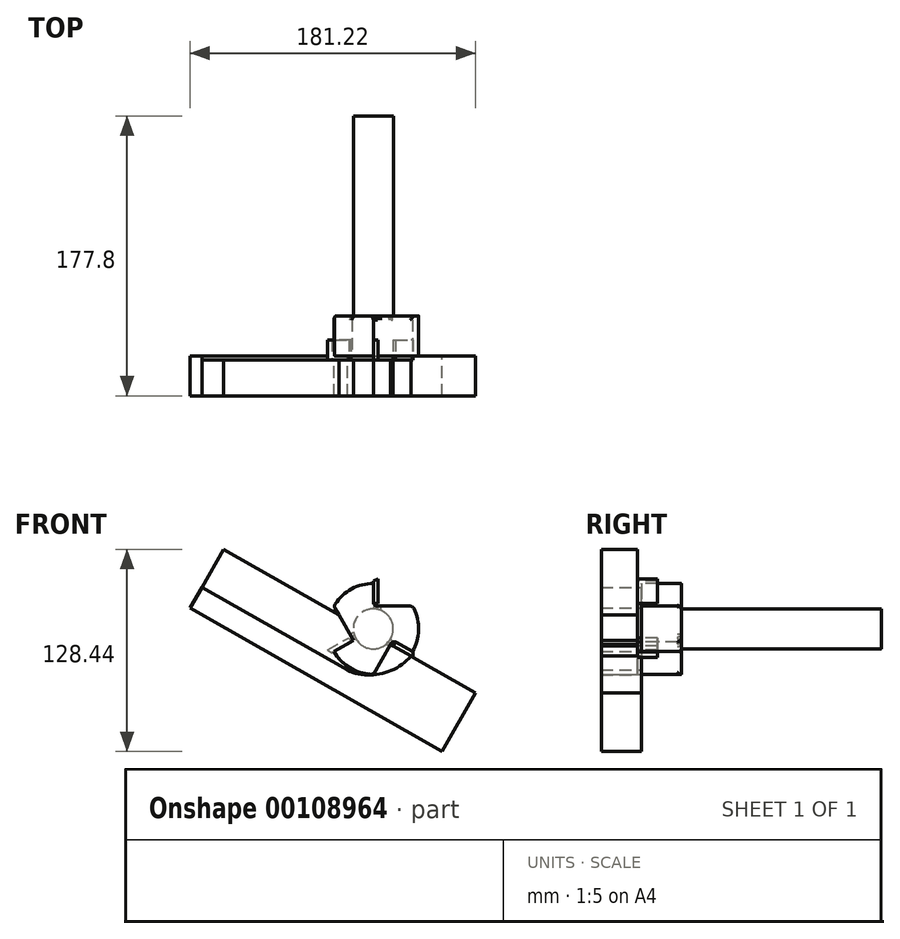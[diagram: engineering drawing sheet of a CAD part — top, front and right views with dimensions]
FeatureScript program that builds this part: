
annotation { "Feature Type Name" : "Feature", "Feature Type Description" : "" }
export const myFeature = defineFeature(function(context is Context, id is Id, definition is map)
    precondition{}
    {
        {
            var Q0;
            Q0=qCreatedBy(makeId("Front.planeOp"),FACE);
            var sketch = newSketch(context, id + "F0", { "sketchPlane" : qUnion([Q0])});
            skArc(sketch, "E0", {"start": v(-24.99, -14.43) * mm, "mid": v(-14.43, -24.99) * mm, "end": v(0, -28.85) * mm});
            skLineSegment(sketch, "E1", {"start": v(0, 14.43) * mm, "end": v(0, 28.85) * mm});
            skLineSegment(sketch, "E2", {"start": v(12.5, -7.21) * mm, "end": v(24.99, -14.43) * mm});
            skLineSegment(sketch, "E3", {"start": v(-12.5, -7.21) * mm, "end": v(-24.99, -14.43) * mm});
            skLineSegment(sketch, "E4", {"start": v(12.5, -7.21) * mm, "end": v(0, -28.85) * mm});
            skLineSegment(sketch, "E5", {"start": v(-12.5, -7.21) * mm, "end": v(-24.99, 14.43) * mm});
            skLineSegment(sketch, "E6", {"start": v(0, 14.43) * mm, "end": v(24.99, 14.43) * mm});
            skArc(sketch, "E7.trimOffspring", {"start": v(24.99, -14.43) * mm, "mid": v(28.85, 0) * mm, "end": v(24.99, 14.43) * mm});
            skArc(sketch, "E8.trimOffspring", {"start": v(0, 28.85) * mm, "mid": v(-14.43, 24.99) * mm, "end": v(-24.99, 14.43) * mm});
            skLineSegment(sketch, "E9", {"start": v(-24.99, -14.43) * mm, "end": v(-26.29, -15.16) * mm});
            skLineSegment(sketch, "E10", {"start": v(-29.06, -13.3) * mm, "end": v(-15.52, -5.64) * mm});
            skLineSegment(sketch, "E11", {"start": v(-15.52, -5.64) * mm, "end": v(-14.1, -8.14) * mm});
            skLineSegment(sketch, "E12", {"start": v(0, 28.85) * mm, "end": v(0, 30.35) * mm});
            skLineSegment(sketch, "E13", {"start": v(3, 31.84) * mm, "end": v(3, 16.29) * mm});
            skLineSegment(sketch, "E14", {"start": v(3, 16.29) * mm, "end": v(0, 16.29) * mm});
            skLineSegment(sketch, "E15", {"start": v(24.99, -14.43) * mm, "end": v(25.36, -14.63) * mm});
            skLineSegment(sketch, "E16", {"start": v(25.18, -17.97) * mm, "end": v(12.56, -10.9) * mm});
            skLineSegment(sketch, "E17", {"start": v(12.56, -10.9) * mm, "end": v(14.1, -8.14) * mm});
            skLineSegment(sketch, "E18", {"start": v(-29.06, -13.3) * mm, "end": v(-26.29, -15.16) * mm});
            skLineSegment(sketch, "E19", {"start": v(25.18, -17.97) * mm, "end": v(25.36, -14.63) * mm});
            skLineSegment(sketch, "E20", {"start": v(3, 31.84) * mm, "end": v(0, 30.35) * mm});
            skLineSegment(sketch, "E21", {"start": v(25.18, -17.97) * mm, "end": v(64.89, -40.59) * mm});
            skLineSegment(sketch, "E22", {"start": v(-16.45, -26.15) * mm, "end": v(-108.78, 26.45) * mm});
            skEllipticalArc(sketch, "E23.trimOffspring", {});
            skLineSegment(sketch, "E24", {"start": v(-108.78, 26.45) * mm, "end": v(-116.33, 13.2) * mm});
            skLineSegment(sketch, "E25", {"start": v(-116.33, 13.2) * mm, "end": v(43.62, -77.92) * mm});
            skLineSegment(sketch, "E26", {"start": v(43.62, -77.92) * mm, "end": v(64.89, -40.59) * mm});
            skLineSegment(sketch, "E27", {"start": v(-108.78, 26.45) * mm, "end": v(-95.06, 50.52) * mm});
            skLineSegment(sketch, "E28", {"start": v(-95.06, 50.52) * mm, "end": v(23.9, -17.25) * mm});
            const initialGuessF0  = {"E23.trimOffspring": [0, 0, -0.9093747763503883, -0.41597778322607715, 0.03196105381302888, 0.028787567373013776, 0.6291453285315938, 2.04370583019782]};
            skSetInitialGuess(sketch, initialGuessF0);
            skSolve(sketch);
        }
        {
            var Q0;
            {var subQ0=sQuery(id+"F0.wireOp",EDGE,"E4");var subQ1=sQuery(id+"F0.wireOp",EDGE,"E0");var subQ2=makeQuery(id+"F0.imprint","INTERSECT",VERTEX,{"derivedFrom":[subQ1,subQ0]});Q0=makeQuery(id+"F0.imprint","IMPRINT",FACE,{"disambiguationData":[TD([[makeQuery(id+"F0.imprint","IMPRINT",EDGE,{"disambiguationData":[TD([[subQ2,1.0]])],"derivedFrom":subQ1}),1.0]])]});}
            var Q1;
            {var subQ11=sQuery(id+"F0.wireOp",EDGE,"E5");Q1=makeQuery(id+"F0.imprint","IMPRINT",FACE,{"disambiguationData":[TD([[makeQuery(id+"F0.imprint","IMPRINT",EDGE,{"derivedFrom":subQ11}),-1.0]])]});}
            var Q2;
            {var subQ0=sQuery(id+"F0.wireOp",EDGE,"E0");var subQ1=sQuery(id+"F0.wireOp",EDGE,"E4");var subQ2=makeQuery(id+"F0.imprint","INTERSECT",VERTEX,{"derivedFrom":[subQ1,subQ0]});Q2=makeQuery(id+"F0.imprint","IMPRINT",FACE,{"disambiguationData":[TD([[makeQuery(id+"F0.imprint","IMPRINT",EDGE,{"disambiguationData":[TD([[subQ2,1.0]])],"derivedFrom":subQ1}),-1.0]])]});}
            var Q3;
            {var subQ3=sQuery(id+"F0.wireOp",EDGE,"E6");Q3=makeQuery(id+"F0.imprint","IMPRINT",FACE,{"disambiguationData":[TD([[makeQuery(id+"F0.imprint","IMPRINT",EDGE,{"derivedFrom":subQ3}),-1.0]])]});}
            extrude(context, id + "F1", {"entities" : qUnion([Q0, Q1, Q2, Q3]), "oppositeDirection" : true, "depth" : 25.4 * mm});
        }
        {
            var Q0;
            {var subQ1=sQuery(id+"F0.wireOp",EDGE,"E15");Q0=makeQuery(id+"F0.imprint","IMPRINT",FACE,{"disambiguationData":[TD([[makeQuery(id+"F0.imprint","IMPRINT",EDGE,{"derivedFrom":subQ1}),-1.0]])]});}
            var Q1;
            {var subQ1=sQuery(id+"F0.wireOp",EDGE,"E12");Q1=makeQuery(id+"F0.imprint","IMPRINT",FACE,{"disambiguationData":[TD([[makeQuery(id+"F0.imprint","IMPRINT",EDGE,{"derivedFrom":subQ1}),-1.0]])]});}
            var Q2;
            {var subQ1=sQuery(id+"F0.wireOp",EDGE,"E9");Q2=makeQuery(id+"F0.imprint","IMPRINT",FACE,{"disambiguationData":[TD([[makeQuery(id+"F0.imprint","IMPRINT",EDGE,{"derivedFrom":subQ1}),-1.0]])]});}
            extrude(context, id + "F2", {"entities" : qUnion([Q0, Q1, Q2]), "oppositeDirection" : true, "depth" : 10.16 * mm, "hasSecondDirection" : true, "secondDirectionOppositeDirection" : false, "secondDirectionDepth" : 2.54 * mm});
        }
        {
            var Q0;
            Q0=makeQuery(id+"F1.opExtrude","CAP_FACE",FACE,{"disambiguationData":[OSD([sQuery(id+"F0.wireOp",EDGE,"E1"),sQuery(id+"F0.wireOp",EDGE,"E2"),sQuery(id+"F0.wireOp",EDGE,"E3"),sQuery(id+"F0.wireOp",EDGE,"E4"),sQuery(id+"F0.wireOp",EDGE,"E5"),sQuery(id+"F0.wireOp",EDGE,"E6"),sQuery(id+"F0.wireOp",EDGE,"E7.trimOffspring"),sQuery(id+"F0.wireOp",EDGE,"E0"),sQuery(id+"F0.wireOp",EDGE,"E8.trimOffspring")])],"isStart":false});
            var sketch = newSketch(context, id + "F3", { "sketchPlane" : qUnion([Q0])});
            skCircle(sketch, "E29", {"center": v(0, 0) * mm, "radius": 12.7 * mm});
            skSolve(sketch);
        }
        {
            var Q0;
            Q0 = qSketchRegion(id + "F3", true);
            var Q1;
            Q1=makeQuery(id+"F3.imprint","IMPRINT",FACE,{"disambiguationData":[TD([[makeQuery(id+"F3.imprint","IMPRINT",EDGE,{"derivedFrom":sQuery(id+"F3.wireOp",EDGE,"E29")}),1.0]])]});
            extrude(context, id + "F4", {"entities" : qUnion([Q0, Q1]), "operationType" : NewBodyOperationType.ADD, "depth" : 127 * mm});
        }
        {
            var Q0;
            Q0=makeQuery(id+"F1.opExtrude","CAP_EDGE",EDGE,{"disambiguationData":[OSD([sQuery(id+"F0.wireOp",EDGE,"E8.trimOffspring")])],"isStart":false});
            var Q1;
            Q1=makeQuery(id+"F1.opExtrude","CAP_EDGE",EDGE,{"disambiguationData":[OSD([sQuery(id+"F0.wireOp",EDGE,"E1")])],"isStart":false});
            var Q2;
            Q2=makeQuery(id+"F1.opExtrude","CAP_EDGE",EDGE,{"disambiguationData":[OSD([sQuery(id+"F0.wireOp",EDGE,"E6")])],"isStart":false});
            var Q3;
            Q3=makeQuery(id+"F1.opExtrude","SWEPT_EDGE",EDGE,{"disambiguationData":[OSD([sQuery(id+"F0.wireOp",EDGE,"E6"),sQuery(id+"F0.wireOp",EDGE,"E7.trimOffspring")])]});
            var Q4;
            Q4=makeQuery(id+"F1.opExtrude","CAP_EDGE",EDGE,{"disambiguationData":[OSD([sQuery(id+"F0.wireOp",EDGE,"E7.trimOffspring")])],"isStart":false});
            var Q5;
            Q5=makeQuery(id+"F1.opExtrude","CAP_EDGE",EDGE,{"disambiguationData":[OSD([sQuery(id+"F0.wireOp",EDGE,"E2")])],"isStart":false});
            var Q6;
            Q6=makeQuery(id+"F1.opExtrude","CAP_EDGE",EDGE,{"disambiguationData":[OSD([sQuery(id+"F0.wireOp",EDGE,"E4")])],"isStart":false});
            var Q7;
            Q7=makeQuery(id+"F1.opExtrude","SWEPT_EDGE",EDGE,{"disambiguationData":[OSD([sQuery(id+"F0.wireOp",EDGE,"E4"),sQuery(id+"F0.wireOp",EDGE,"E0")])]});
            var Q8;
            Q8=makeQuery(id+"F1.opExtrude","CAP_EDGE",EDGE,{"disambiguationData":[OSD([sQuery(id+"F0.wireOp",EDGE,"E0")])],"isStart":false});
            var Q9;
            Q9=makeQuery(id+"F1.opExtrude","SWEPT_EDGE",EDGE,{"disambiguationData":[OSD([sQuery(id+"F0.wireOp",EDGE,"E5"),sQuery(id+"F0.wireOp",EDGE,"E8.trimOffspring")])]});
            var Q10;
            Q10=makeQuery(id+"F1.opExtrude","CAP_EDGE",EDGE,{"disambiguationData":[OSD([sQuery(id+"F0.wireOp",EDGE,"E5")])],"isStart":false});
            var Q11;
            Q11=makeQuery(id+"F1.opExtrude","CAP_EDGE",EDGE,{"disambiguationData":[OSD([sQuery(id+"F0.wireOp",EDGE,"E3")])],"isStart":false});
            fillet(context, id + "F5", {"entities" : qUnion([Q0, Q1, Q2, Q3, Q4, Q5, Q6, Q7, Q8, Q9, Q10, Q11]), "radius" : 2.54 * mm, "tangentPropagation" : true, "allowEdgeOverflow" : false});
        }
        {
            var Q0;
            Q0=makeQuery(id+"F0.imprint","IMPRINT",FACE,{"disambiguationData":[TD([[makeQuery(id+"F0.imprint","IMPRINT",EDGE,{"derivedFrom":sQuery(id+"F0.wireOp",EDGE,"E16")}),1.0]])]});
            extrude(context, id + "F6", {"entities" : qUnion([Q0]), "operationType" : NewBodyOperationType.ADD, "depth" : 25.4 * mm});
        }
        {
            var Q0;
            Q0=makeQuery(id+"F0.imprint","IMPRINT",FACE,{"disambiguationData":[TD([[makeQuery(id+"F0.imprint","IMPRINT",EDGE,{"derivedFrom":sQuery(id+"F0.wireOp",EDGE,"E9")}),1.0]])]});
            var Q1;
            {var subQ5=sQuery(id+"F0.wireOp",EDGE,"E0");Q1=makeQuery(id+"F0.imprint","IMPRINT",FACE,{"disambiguationData":[TD([[makeQuery(id+"F0.imprint","IMPRINT",EDGE,{"derivedFrom":subQ5}),1.0]])]});}
            var Q2;
            {var subQ1=sQuery(id+"F0.wireOp",EDGE,"E9");Q2=makeQuery(id+"F0.imprint","IMPRINT",FACE,{"disambiguationData":[TD([[makeQuery(id+"F0.imprint","IMPRINT",EDGE,{"derivedFrom":subQ1}),-1.0]])]});}
            extrude(context, id + "F7", {"entities" : qUnion([Q0, Q1, Q2]), "depth" : 25.4 * mm, "hasSecondDirection" : true, "secondDirectionOppositeDirection" : false, "secondDirectionDepth" : 2.54 * mm});
        }
    });
